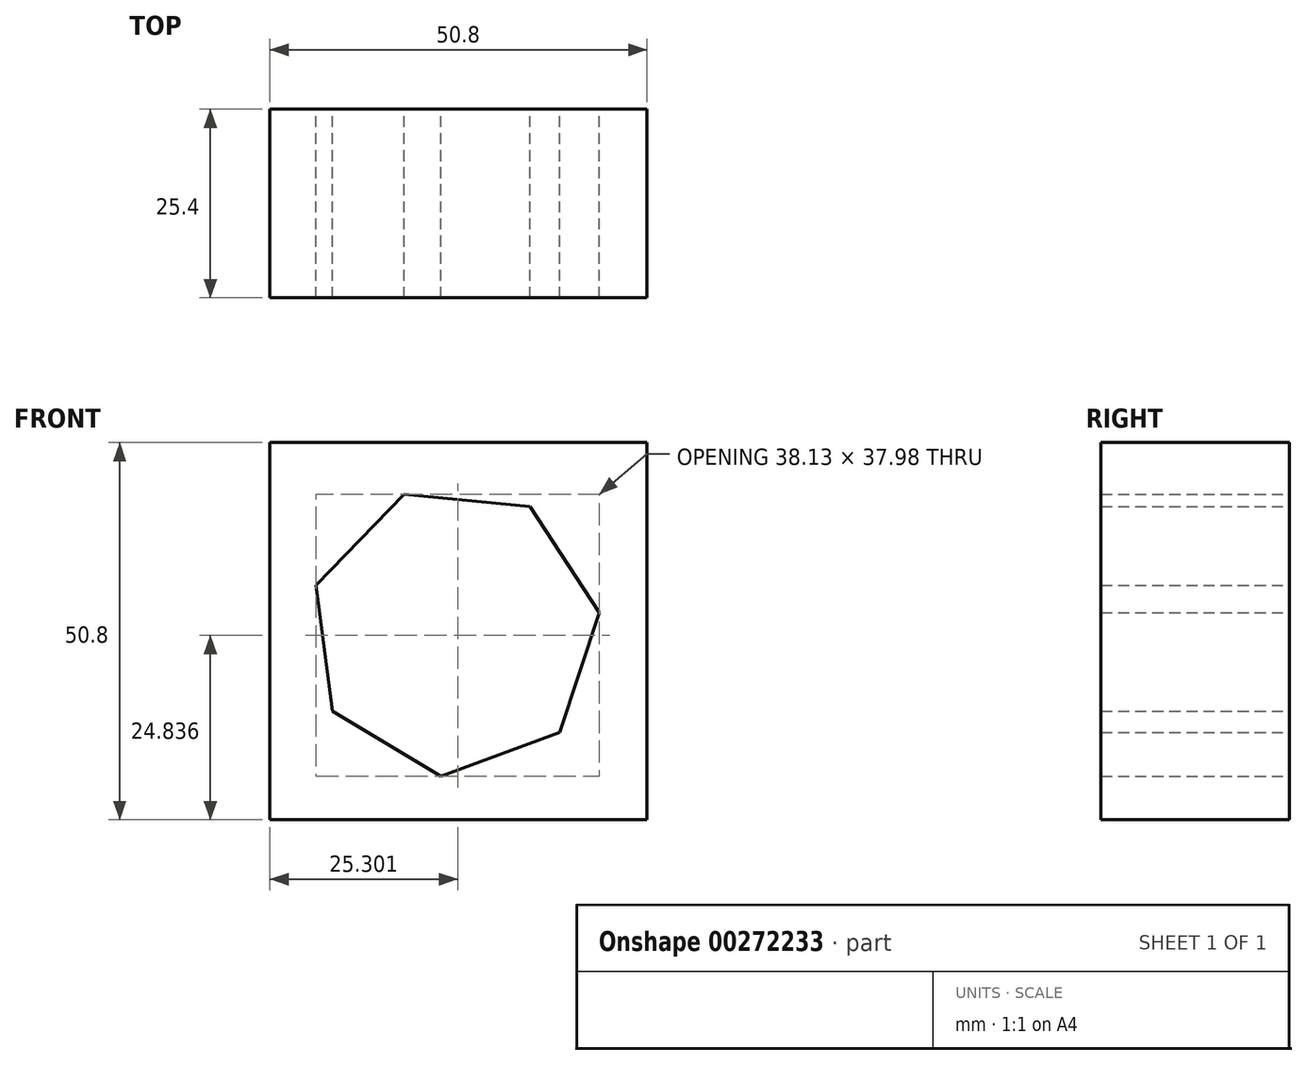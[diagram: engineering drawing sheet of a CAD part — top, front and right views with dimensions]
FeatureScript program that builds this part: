
annotation { "Feature Type Name" : "Feature", "Feature Type Description" : "" }
export const myFeature = defineFeature(function(context is Context, id is Id, definition is map)
    precondition{}
    {
        {
            var Q0;
            Q0=qCreatedBy(makeId("Front.planeOp"),FACE);
            var sketch = newSketch(context, id + "F0", { "sketchPlane" : qUnion([Q0])});
            skLineSegment(sketch, "E0.bottom", {"start": v(-22.56, 25.4) * mm, "end": v(28.24, 25.4) * mm});
            skLineSegment(sketch, "E0.top", {"start": v(-22.56, -25.4) * mm, "end": v(28.24, -25.4) * mm});
            skLineSegment(sketch, "E0.left", {"start": v(-22.56, 25.4) * mm, "end": v(-22.56, -25.4) * mm});
            skLineSegment(sketch, "E0.right", {"start": v(28.24, 25.4) * mm, "end": v(28.24, -25.4) * mm});
            skCircle(sketch, "E1", {"center": v(2.33, 0) * mm, "radius": 22.86 * mm});
            skCircle(sketch, "E2.cCircle", {"center": v(2.33, 0) * mm, "radius": 17.7 * mm, "construction": true});
            skLineSegment(sketch, "E2.0", {"start": v(21.8, 2.53) * mm, "end": v(16.45, -13.65) * mm});
            skLineSegment(sketch, "E2.1", {"start": v(16.45, -13.65) * mm, "end": v(0.46, -19.56) * mm});
            skLineSegment(sketch, "E2.2", {"start": v(0.46, -19.56) * mm, "end": v(-14.12, -10.74) * mm});
            skLineSegment(sketch, "E2.3", {"start": v(-14.12, -10.74) * mm, "end": v(-16.32, 6.17) * mm});
            skLineSegment(sketch, "E2.4", {"start": v(-16.32, 6.17) * mm, "end": v(-4.48, 18.43) * mm});
            skLineSegment(sketch, "E2.5", {"start": v(-4.48, 18.43) * mm, "end": v(12.5, 16.81) * mm});
            skLineSegment(sketch, "E2.6", {"start": v(12.5, 16.81) * mm, "end": v(21.8, 2.53) * mm});
            skPoint(sketch, "E2.0.midPoint", {"position": v(19.13, -5.56) * mm});
            skSolve(sketch);
        }
        {
            var Q0;
            Q0 = qSketchRegion(id + "F0", true);
            var Q1;
            Q1=makeQuery(id+"F0.imprint","IMPRINT",FACE,{"disambiguationData":[TD([[makeQuery(id+"F0.imprint","IMPRINT",EDGE,{"derivedFrom":sQuery(id+"F0.wireOp",EDGE,"E1")}),1.0]])]});
            extrude(context, id + "F1", {"entities" : qUnion([Q0, Q1]), "depth" : 25.4 * mm});
        }
    });
